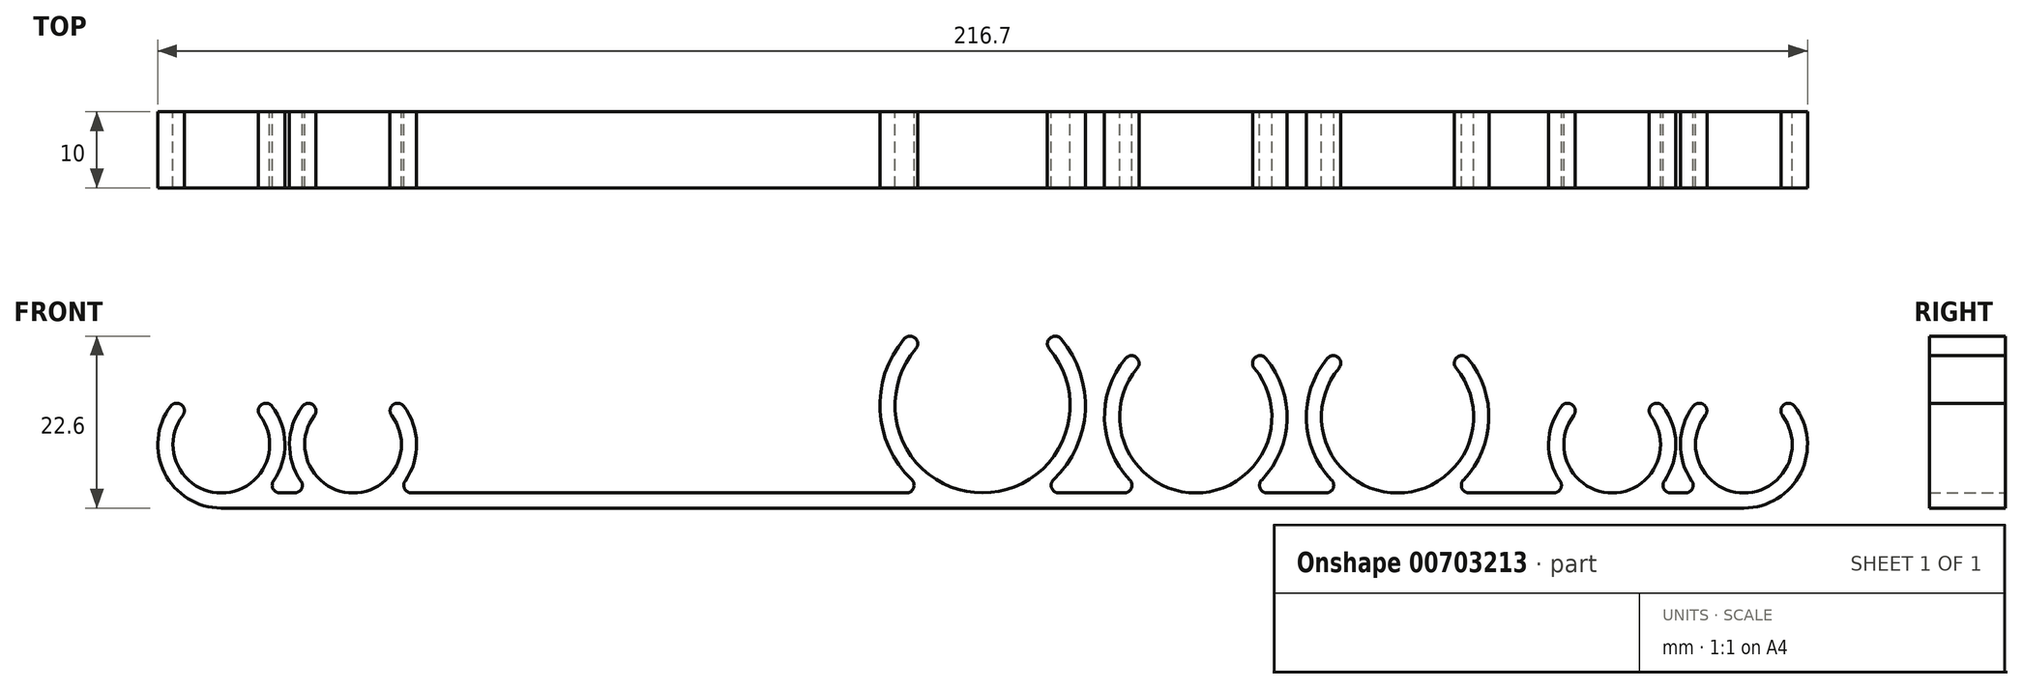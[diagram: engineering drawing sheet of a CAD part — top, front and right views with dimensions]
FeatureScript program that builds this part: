
annotation { "Feature Type Name" : "Feature", "Feature Type Description" : "" }
export const myFeature = defineFeature(function(context is Context, id is Id, definition is map)
    precondition{}
    {
        {
            var Q0;
            Q0=qCreatedBy(makeId("Front.planeOp"),FACE);
            var sketch = newSketch(context, id + "F0", { "sketchPlane" : qUnion([Q0])});
            skLineSegment(sketch, "E0", {"start": v(0, 0) * mm, "end": v(-100, 0) * mm});
            skLineSegment(sketch, "E1", {"start": v(0, 0) * mm, "end": v(100, 0) * mm});
            skArc(sketch, "E2", {"start": v(-10.28, 22.25) * mm, "mid": v(-13.48, 12.8) * mm, "end": v(-9.31, 3.72) * mm});
            skPoint(sketch, "E2.second.point", {"position": v(-7, 25.04) * mm});
            skPoint(sketch, "E2.third.point", {"position": v(7, 25.04) * mm});
            skArc(sketch, "E3", {"start": v(-8.76, 20.96) * mm, "mid": v(0, 2) * mm, "end": v(8.76, 20.96) * mm});
            skArc(sketch, "E4", {"start": v(93.35, 13.4) * mm, "mid": v(91.65, 8.52) * mm, "end": v(93.15, 3.57) * mm});
            skArc(sketch, "E5", {"start": v(94.94, 12.19) * mm, "mid": v(100, 2) * mm, "end": v(105.06, 12.19) * mm});
            skLineSegment(sketch, "E6", {"start": v(105.15, 13.5) * mm, "end": v(105.15, 13.5) * mm});
            skLineSegment(sketch, "E7", {"start": v(100, 8.35) * mm, "end": v(100, 22.96) * mm});
            skLineSegment(sketch, "E8", {"start": v(94.85, 13.5) * mm, "end": v(94.85, 13.5) * mm});
            skPoint(sketch, "E9.visualSharp", {"position": v(94.1, 14.25) * mm});
            skArc(sketch, "E9.filletArc", {"start": v(94.85, 13.5) * mm, "mid": v(94.08, 13.79) * mm, "end": v(93.35, 13.4) * mm});
            skArc(sketch, "E10.filletArc", {"start": v(94.94, 12.19) * mm, "mid": v(95.14, 12.86) * mm, "end": v(94.85, 13.5) * mm});
            skArc(sketch, "E11.filletArc", {"start": v(105.15, 13.5) * mm, "mid": v(104.86, 12.86) * mm, "end": v(105.06, 12.19) * mm});
            skPoint(sketch, "E12.visualSharp", {"position": v(105.9, 14.25) * mm});
            skArc(sketch, "E12.filletArc", {"start": v(106.65, 13.4) * mm, "mid": v(105.92, 13.79) * mm, "end": v(105.15, 13.5) * mm});
            skArc(sketch, "E13", {"start": v(76.05, 13.4) * mm, "mid": v(74.35, 8.52) * mm, "end": v(75.85, 3.57) * mm});
            skArc(sketch, "E14", {"start": v(77.64, 12.19) * mm, "mid": v(82.7, 2) * mm, "end": v(87.76, 12.19) * mm});
            skLineSegment(sketch, "E15", {"start": v(82.7, 8.35) * mm, "end": v(82.7, 27.75) * mm});
            skLineSegment(sketch, "E16", {"start": v(87.85, 13.5) * mm, "end": v(87.85, 13.5) * mm});
            skLineSegment(sketch, "E17", {"start": v(77.55, 13.5) * mm, "end": v(77.55, 13.5) * mm});
            skPoint(sketch, "E18.visualSharp", {"position": v(76.8, 14.25) * mm});
            skArc(sketch, "E18.filletArc", {"start": v(77.55, 13.5) * mm, "mid": v(76.78, 13.79) * mm, "end": v(76.05, 13.4) * mm});
            skArc(sketch, "E19.filletArc", {"start": v(77.64, 12.19) * mm, "mid": v(77.84, 12.86) * mm, "end": v(77.55, 13.5) * mm});
            skArc(sketch, "E20.filletArc", {"start": v(87.85, 13.5) * mm, "mid": v(87.56, 12.86) * mm, "end": v(87.76, 12.19) * mm});
            skPoint(sketch, "E21.visualSharp", {"position": v(88.6, 14.25) * mm});
            skArc(sketch, "E21.filletArc", {"start": v(89.35, 13.4) * mm, "mid": v(88.62, 13.79) * mm, "end": v(87.85, 13.5) * mm});
            skArc(sketch, "E22", {"start": v(18.78, 19.68) * mm, "mid": v(16, 11.58) * mm, "end": v(19.34, 3.7) * mm});
            skArc(sketch, "E23", {"start": v(20.32, 18.4) * mm, "mid": v(28, 2) * mm, "end": v(35.68, 18.4) * mm});
            skArc(sketch, "E24", {"start": v(45.28, 19.68) * mm, "mid": v(42.5, 11.58) * mm, "end": v(45.84, 3.7) * mm});
            skArc(sketch, "E25", {"start": v(46.82, 18.4) * mm, "mid": v(54.5, 2) * mm, "end": v(62.18, 18.4) * mm});
            skLineSegment(sketch, "E26", {"start": v(28, 12) * mm, "end": v(28, 43.28) * mm});
            skLineSegment(sketch, "E27", {"start": v(-8.81, 22.31) * mm, "end": v(-8.81, 22.31) * mm});
            skLineSegment(sketch, "E28", {"start": v(8.81, 22.31) * mm, "end": v(8.81, 22.31) * mm});
            skLineSegment(sketch, "E29", {"start": v(20.25, 19.75) * mm, "end": v(20.25, 19.75) * mm});
            skLineSegment(sketch, "E30", {"start": v(35.75, 19.75) * mm, "end": v(35.75, 19.75) * mm});
            skLineSegment(sketch, "E31", {"start": v(62.25, 19.75) * mm, "end": v(62.25, 19.75) * mm});
            skLineSegment(sketch, "E32", {"start": v(46.75, 19.75) * mm, "end": v(46.75, 19.75) * mm});
            skArc(sketch, "E33.filletArc", {"start": v(46.82, 18.4) * mm, "mid": v(47.05, 19.08) * mm, "end": v(46.75, 19.75) * mm});
            skPoint(sketch, "E34.visualSharp", {"position": v(46.01, 20.49) * mm});
            skArc(sketch, "E34.filletArc", {"start": v(46.75, 19.75) * mm, "mid": v(46, 20.04) * mm, "end": v(45.28, 19.68) * mm});
            skPoint(sketch, "E35.visualSharp", {"position": v(62.99, 20.49) * mm});
            skArc(sketch, "E35.filletArc", {"start": v(63.72, 19.68) * mm, "mid": v(63, 20.04) * mm, "end": v(62.25, 19.75) * mm});
            skArc(sketch, "E36.filletArc", {"start": v(62.25, 19.75) * mm, "mid": v(61.95, 19.08) * mm, "end": v(62.18, 18.4) * mm});
            skPoint(sketch, "E37.visualSharp", {"position": v(36.49, 20.49) * mm});
            skArc(sketch, "E37.filletArc", {"start": v(37.22, 19.68) * mm, "mid": v(36.5, 20.04) * mm, "end": v(35.75, 19.75) * mm});
            skArc(sketch, "E38.filletArc", {"start": v(35.75, 19.75) * mm, "mid": v(35.45, 19.08) * mm, "end": v(35.68, 18.4) * mm});
            skPoint(sketch, "E39.visualSharp", {"position": v(19.51, 20.49) * mm});
            skArc(sketch, "E39.filletArc", {"start": v(20.25, 19.75) * mm, "mid": v(19.5, 20.04) * mm, "end": v(18.78, 19.68) * mm});
            skPoint(sketch, "E40.visualSharp", {"position": v(20.93, 19.07) * mm});
            skArc(sketch, "E40.filletArc", {"start": v(20.32, 18.4) * mm, "mid": v(20.55, 19.08) * mm, "end": v(20.25, 19.75) * mm});
            skPoint(sketch, "E41.visualSharp", {"position": v(9.55, 23.05) * mm});
            skArc(sketch, "E41.filletArc", {"start": v(10.28, 22.25) * mm, "mid": v(9.56, 22.6) * mm, "end": v(8.81, 22.31) * mm});
            skPoint(sketch, "E42.visualSharp", {"position": v(8.13, 21.63) * mm});
            skArc(sketch, "E42.filletArc", {"start": v(8.81, 22.31) * mm, "mid": v(8.52, 21.64) * mm, "end": v(8.76, 20.96) * mm});
            skPoint(sketch, "E43.visualSharp", {"position": v(-9.55, 23.05) * mm});
            skArc(sketch, "E43.filletArc", {"start": v(-8.81, 22.31) * mm, "mid": v(-9.56, 22.6) * mm, "end": v(-10.28, 22.25) * mm});
            skPoint(sketch, "E44.visualSharp", {"position": v(-8.13, 21.63) * mm});
            skArc(sketch, "E44.filletArc", {"start": v(-8.76, 20.96) * mm, "mid": v(-8.52, 21.64) * mm, "end": v(-8.81, 22.31) * mm});
            skLineSegment(sketch, "E45", {"start": v(92.33, 2) * mm, "end": v(90.37, 2) * mm});
            skArc(sketch, "E46", {"start": v(-105.06, 12.19) * mm, "mid": v(-100, 2) * mm, "end": v(-94.94, 12.19) * mm});
            skArc(sketch, "E47", {"start": v(-106.65, 13.4) * mm, "mid": v(-107.48, 4.64) * mm, "end": v(-100, 0) * mm});
            skLineSegment(sketch, "E48", {"start": v(-100, 14.7) * mm, "end": v(-100, 16.7) * mm});
            skLineSegment(sketch, "E49", {"start": v(-94.85, 13.5) * mm, "end": v(-94.85, 13.5) * mm});
            skLineSegment(sketch, "E50", {"start": v(-105.15, 13.5) * mm, "end": v(-105.15, 13.5) * mm});
            skArc(sketch, "E51", {"start": v(-89.36, 13.38) * mm, "mid": v(-91.05, 8.5) * mm, "end": v(-89.55, 3.57) * mm});
            skArc(sketch, "E52", {"start": v(-87.77, 12.18) * mm, "mid": v(-82.7, 2) * mm, "end": v(-77.64, 12.19) * mm});
            skLineSegment(sketch, "E53", {"start": v(-77.55, 13.5) * mm, "end": v(-77.55, 13.5) * mm});
            skLineSegment(sketch, "E54", {"start": v(-87.86, 13.49) * mm, "end": v(-87.86, 13.49) * mm});
            skPoint(sketch, "E55.visualSharp", {"position": v(-105.9, 14.25) * mm});
            skArc(sketch, "E55.filletArc", {"start": v(-105.15, 13.5) * mm, "mid": v(-105.92, 13.79) * mm, "end": v(-106.65, 13.4) * mm});
            skArc(sketch, "E56.filletArc", {"start": v(-105.06, 12.19) * mm, "mid": v(-104.86, 12.86) * mm, "end": v(-105.15, 13.5) * mm});
            skArc(sketch, "E57.filletArc", {"start": v(-94.85, 13.5) * mm, "mid": v(-95.14, 12.86) * mm, "end": v(-94.94, 12.19) * mm});
            skPoint(sketch, "E58.visualSharp", {"position": v(-94.1, 14.25) * mm});
            skArc(sketch, "E58.filletArc", {"start": v(-93.35, 13.4) * mm, "mid": v(-94.08, 13.79) * mm, "end": v(-94.85, 13.5) * mm});
            skPoint(sketch, "E59.visualSharp", {"position": v(-88.61, 14.24) * mm});
            skArc(sketch, "E59.filletArc", {"start": v(-87.86, 13.49) * mm, "mid": v(-88.63, 13.78) * mm, "end": v(-89.36, 13.38) * mm});
            skArc(sketch, "E60.filletArc", {"start": v(-87.77, 12.18) * mm, "mid": v(-87.57, 12.85) * mm, "end": v(-87.86, 13.49) * mm});
            skPoint(sketch, "E61.visualSharp", {"position": v(-76.8, 14.25) * mm});
            skArc(sketch, "E61.filletArc", {"start": v(-76.05, 13.4) * mm, "mid": v(-76.78, 13.79) * mm, "end": v(-77.55, 13.5) * mm});
            skArc(sketch, "E62.filletArc", {"start": v(-77.55, 13.5) * mm, "mid": v(-77.84, 12.86) * mm, "end": v(-77.64, 12.19) * mm});
            skPoint(sketch, "E63.orphan", {"position": v(-100, 2) * mm});
            skLineSegment(sketch, "E64.trimOffspring", {"start": v(-90.37, 2) * mm, "end": v(-92.33, 2) * mm});
            skArc(sketch, "E65.trimOffspring", {"start": v(-75.85, 3.57) * mm, "mid": v(-74.35, 8.52) * mm, "end": v(-76.05, 13.4) * mm});
            skArc(sketch, "E66.trimOffspring", {"start": v(-93.15, 3.57) * mm, "mid": v(-91.65, 8.52) * mm, "end": v(-93.35, 13.4) * mm});
            skArc(sketch, "E67.trimOffspring", {"start": v(9.31, 3.72) * mm, "mid": v(13.48, 12.8) * mm, "end": v(10.28, 22.25) * mm});
            skLineSegment(sketch, "E68.trimOffspring", {"start": v(-10, 2) * mm, "end": v(-75.03, 2) * mm});
            skLineSegment(sketch, "E69.trimOffspring", {"start": v(18.62, 2) * mm, "end": v(10, 2) * mm});
            skArc(sketch, "E70.trimOffspring", {"start": v(36.66, 3.7) * mm, "mid": v(40, 11.58) * mm, "end": v(37.22, 19.68) * mm});
            skPoint(sketch, "E71.visualSharp", {"position": v(-94.58, 2) * mm});
            skArc(sketch, "E71.filletArc", {"start": v(-93.15, 3.57) * mm, "mid": v(-93.22, 2.54) * mm, "end": v(-92.33, 2) * mm});
            skPoint(sketch, "E72.visualSharp", {"position": v(-88.12, 2) * mm});
            skArc(sketch, "E72.filletArc", {"start": v(-90.37, 2) * mm, "mid": v(-89.48, 2.54) * mm, "end": v(-89.55, 3.57) * mm});
            skPoint(sketch, "E73.visualSharp", {"position": v(-77.28, 2) * mm});
            skArc(sketch, "E73.filletArc", {"start": v(-75.85, 3.57) * mm, "mid": v(-75.92, 2.54) * mm, "end": v(-75.03, 2) * mm});
            skPoint(sketch, "E74.visualSharp", {"position": v(-7.07, 2) * mm});
            skArc(sketch, "E74.filletArc", {"start": v(-10, 2) * mm, "mid": v(-9.07, 2.63) * mm, "end": v(-9.31, 3.72) * mm});
            skPoint(sketch, "E75.visualSharp", {"position": v(21.37, 2) * mm});
            skArc(sketch, "E75.filletArc", {"start": v(18.62, 2) * mm, "mid": v(19.54, 2.6) * mm, "end": v(19.34, 3.7) * mm});
            skPoint(sketch, "E76.visualSharp", {"position": v(7.07, 2) * mm});
            skArc(sketch, "E76.filletArc", {"start": v(9.31, 3.72) * mm, "mid": v(9.07, 2.63) * mm, "end": v(10, 2) * mm});
            skArc(sketch, "E77.filletArc", {"start": v(36.66, 3.7) * mm, "mid": v(36.46, 2.6) * mm, "end": v(37.38, 2) * mm});
            skLineSegment(sketch, "E78.trimOffspring", {"start": v(45.12, 2) * mm, "end": v(37.38, 2) * mm});
            skArc(sketch, "E79.trimOffspring", {"start": v(63.16, 3.7) * mm, "mid": v(66.5, 11.58) * mm, "end": v(63.72, 19.68) * mm});
            skLineSegment(sketch, "E80.trimOffspring", {"start": v(75.03, 2) * mm, "end": v(63.88, 2) * mm});
            skArc(sketch, "E81.trimOffspring", {"start": v(89.55, 3.57) * mm, "mid": v(91.05, 8.52) * mm, "end": v(89.35, 13.4) * mm});
            skPoint(sketch, "E82.orphan", {"position": v(100, 2) * mm});
            skArc(sketch, "E83.trimOffspring", {"start": v(100, 0) * mm, "mid": v(107.48, 4.64) * mm, "end": v(106.65, 13.4) * mm});
            skPoint(sketch, "E84.visualSharp", {"position": v(47.87, 2) * mm});
            skArc(sketch, "E84.filletArc", {"start": v(45.12, 2) * mm, "mid": v(46.04, 2.6) * mm, "end": v(45.84, 3.7) * mm});
            skPoint(sketch, "E85.visualSharp", {"position": v(77.28, 2) * mm});
            skArc(sketch, "E85.filletArc", {"start": v(75.03, 2) * mm, "mid": v(75.92, 2.54) * mm, "end": v(75.85, 3.57) * mm});
            skPoint(sketch, "E86.visualSharp", {"position": v(61.13, 2) * mm});
            skArc(sketch, "E86.filletArc", {"start": v(63.16, 3.7) * mm, "mid": v(62.96, 2.6) * mm, "end": v(63.88, 2) * mm});
            skPoint(sketch, "E87.visualSharp", {"position": v(88.12, 2) * mm});
            skArc(sketch, "E87.filletArc", {"start": v(89.55, 3.57) * mm, "mid": v(89.48, 2.54) * mm, "end": v(90.37, 2) * mm});
            skPoint(sketch, "E88.visualSharp", {"position": v(94.58, 2) * mm});
            skArc(sketch, "E88.filletArc", {"start": v(92.33, 2) * mm, "mid": v(93.22, 2.54) * mm, "end": v(93.15, 3.57) * mm});
            skSolve(sketch);
        }
        {
            var Q0;
            Q0 = qSketchRegion(id + "F0", true);
            extrude(context, id + "F1", {"entities" : qUnion([Q0]), "depth" : 10 * mm, "offsetDistance" : 25 * mm});
        }
    });
